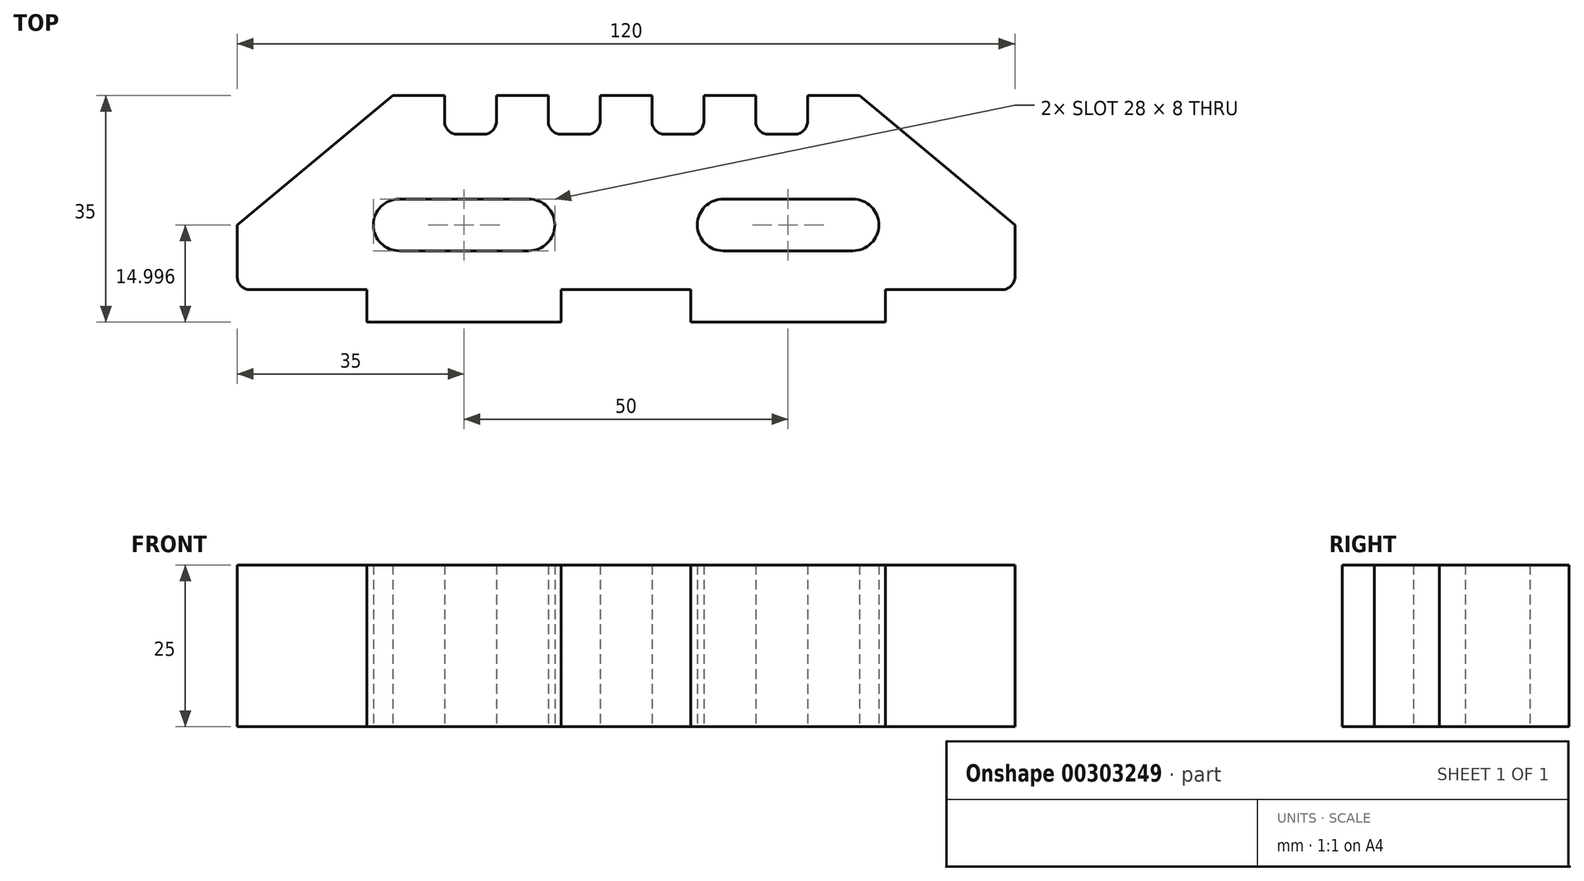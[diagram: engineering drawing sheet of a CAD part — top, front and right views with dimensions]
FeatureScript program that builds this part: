
annotation { "Feature Type Name" : "Feature", "Feature Type Description" : "" }
export const myFeature = defineFeature(function(context is Context, id is Id, definition is map)
    precondition{}
    {
        {
            var Q0;
            Q0=qCreatedBy(makeId("Top.planeOp"),FACE);
            var sketch = newSketch(context, id + "F0", { "sketchPlane" : qUnion([Q0])});
            skLineSegment(sketch, "E0", {"start": v(-58, -43.37) * mm, "end": v(-40, -43.37) * mm});
            skLineSegment(sketch, "E1", {"start": v(-40, -43.37) * mm, "end": v(-40, -48.37) * mm});
            skLineSegment(sketch, "E2", {"start": v(-40, -48.37) * mm, "end": v(-10, -48.37) * mm});
            skLineSegment(sketch, "E3", {"start": v(-10, -48.37) * mm, "end": v(-10, -43.37) * mm});
            skLineSegment(sketch, "E4", {"start": v(-10, -43.37) * mm, "end": v(10, -43.37) * mm});
            skLineSegment(sketch, "E5", {"start": v(10, -43.37) * mm, "end": v(10, -48.37) * mm});
            skLineSegment(sketch, "E6", {"start": v(10, -48.37) * mm, "end": v(40, -48.37) * mm});
            skLineSegment(sketch, "E7", {"start": v(40, -48.37) * mm, "end": v(40, -43.37) * mm});
            skLineSegment(sketch, "E8", {"start": v(40, -43.37) * mm, "end": v(58, -43.37) * mm});
            skLineSegment(sketch, "E9", {"start": v(60, -41.37) * mm, "end": v(60, -33.37) * mm});
            skLineSegment(sketch, "E10", {"start": v(36, -13.37) * mm, "end": v(60, -33.37) * mm});
            skLineSegment(sketch, "E11", {"start": v(36, -13.37) * mm, "end": v(28, -13.37) * mm});
            skLineSegment(sketch, "E12", {"start": v(28, -13.37) * mm, "end": v(28, -17.37) * mm});
            skLineSegment(sketch, "E13", {"start": v(26, -19.37) * mm, "end": v(22, -19.37) * mm});
            skLineSegment(sketch, "E14", {"start": v(20, -17.37) * mm, "end": v(20, -13.37) * mm});
            skLineSegment(sketch, "E15", {"start": v(20, -13.37) * mm, "end": v(12, -13.37) * mm});
            skLineSegment(sketch, "E16", {"start": v(12, -13.37) * mm, "end": v(12, -17.37) * mm});
            skLineSegment(sketch, "E17", {"start": v(10, -19.37) * mm, "end": v(6, -19.37) * mm});
            skLineSegment(sketch, "E18", {"start": v(4, -17.37) * mm, "end": v(4, -13.37) * mm});
            skLineSegment(sketch, "E19", {"start": v(4, -13.37) * mm, "end": v(-4, -13.37) * mm});
            skLineSegment(sketch, "E20", {"start": v(-4, -13.37) * mm, "end": v(-4, -17.37) * mm});
            skLineSegment(sketch, "E21", {"start": v(-6, -19.37) * mm, "end": v(-10, -19.37) * mm});
            skLineSegment(sketch, "E22", {"start": v(-12, -17.37) * mm, "end": v(-12, -13.37) * mm});
            skLineSegment(sketch, "E23", {"start": v(-12, -13.37) * mm, "end": v(-20, -13.37) * mm});
            skLineSegment(sketch, "E24", {"start": v(-20, -13.37) * mm, "end": v(-20, -17.37) * mm});
            skLineSegment(sketch, "E25", {"start": v(-22, -19.37) * mm, "end": v(-26, -19.37) * mm});
            skLineSegment(sketch, "E26", {"start": v(-28, -17.37) * mm, "end": v(-28, -13.37) * mm});
            skLineSegment(sketch, "E27", {"start": v(-28, -13.37) * mm, "end": v(-36, -13.37) * mm});
            skLineSegment(sketch, "E28", {"start": v(-60, -41.37) * mm, "end": v(-60, -33.37) * mm});
            skLineSegment(sketch, "E29", {"start": v(-60, -33.37) * mm, "end": v(-36, -13.37) * mm});
            skPoint(sketch, "E30.visualSharp", {"position": v(-28, -19.37) * mm});
            skArc(sketch, "E30.filletArc", {"start": v(-28, -17.37) * mm, "mid": v(-27.41, -18.79) * mm, "end": v(-26, -19.37) * mm});
            skPoint(sketch, "E31.visualSharp", {"position": v(-20, -19.37) * mm});
            skArc(sketch, "E31.filletArc", {"start": v(-22, -19.37) * mm, "mid": v(-20.59, -18.79) * mm, "end": v(-20, -17.37) * mm});
            skPoint(sketch, "E32.visualSharp", {"position": v(-12, -19.37) * mm});
            skArc(sketch, "E32.filletArc", {"start": v(-12, -17.37) * mm, "mid": v(-11.41, -18.79) * mm, "end": v(-10, -19.37) * mm});
            skPoint(sketch, "E33.visualSharp", {"position": v(-4, -19.37) * mm});
            skArc(sketch, "E33.filletArc", {"start": v(-6, -19.37) * mm, "mid": v(-4.59, -18.79) * mm, "end": v(-4, -17.37) * mm});
            skPoint(sketch, "E34.visualSharp", {"position": v(4, -19.37) * mm});
            skArc(sketch, "E34.filletArc", {"start": v(4, -17.37) * mm, "mid": v(4.59, -18.79) * mm, "end": v(6, -19.37) * mm});
            skPoint(sketch, "E35.visualSharp", {"position": v(12, -19.37) * mm});
            skArc(sketch, "E35.filletArc", {"start": v(10, -19.37) * mm, "mid": v(11.41, -18.79) * mm, "end": v(12, -17.37) * mm});
            skPoint(sketch, "E36.visualSharp", {"position": v(20, -19.37) * mm});
            skArc(sketch, "E36.filletArc", {"start": v(20, -17.37) * mm, "mid": v(20.59, -18.79) * mm, "end": v(22, -19.37) * mm});
            skPoint(sketch, "E37.visualSharp", {"position": v(28, -19.37) * mm});
            skArc(sketch, "E37.filletArc", {"start": v(26, -19.37) * mm, "mid": v(27.41, -18.79) * mm, "end": v(28, -17.37) * mm});
            skPoint(sketch, "E38.visualSharp", {"position": v(60, -43.37) * mm});
            skArc(sketch, "E38.filletArc", {"start": v(58, -43.37) * mm, "mid": v(59.41, -42.79) * mm, "end": v(60, -41.37) * mm});
            skPoint(sketch, "E39.visualSharp", {"position": v(-60, -43.37) * mm});
            skArc(sketch, "E39.filletArc", {"start": v(-60, -41.37) * mm, "mid": v(-59.41, -42.79) * mm, "end": v(-58, -43.37) * mm});
            skLineSegment(sketch, "E40", {"start": v(11, -29.37) * mm, "end": v(39, -29.37) * mm});
            skLineSegment(sketch, "E41", {"start": v(35, -29.37) * mm, "end": v(15, -29.37) * mm});
            skLineSegment(sketch, "E42", {"start": v(11, -33.37) * mm, "end": v(11, -33.37) * mm});
            skLineSegment(sketch, "E43", {"start": v(15, -37.37) * mm, "end": v(35, -37.37) * mm});
            skLineSegment(sketch, "E44", {"start": v(39, -33.37) * mm, "end": v(39, -33.37) * mm});
            skPoint(sketch, "E45.orphan", {"position": v(25, -29.37) * mm});
            skPoint(sketch, "E46.start.orphan", {"position": v(25, -48.37) * mm});
            skPoint(sketch, "E47.orphan", {"position": v(0, -29.37) * mm});
            skPoint(sketch, "E48.orphan", {"position": v(0, -43.37) * mm});
            skPoint(sketch, "E49.end.orphan", {"position": v(0, -13.37) * mm});
            skLineSegment(sketch, "E50", {"start": v(-11, -29.37) * mm, "end": v(-39, -29.37) * mm});
            skLineSegment(sketch, "E51", {"start": v(-39, -33.37) * mm, "end": v(-39, -33.37) * mm});
            skLineSegment(sketch, "E52", {"start": v(-35, -29.37) * mm, "end": v(-15, -29.37) * mm});
            skLineSegment(sketch, "E53", {"start": v(-11, -33.37) * mm, "end": v(-11, -33.37) * mm});
            skPoint(sketch, "E54.end.orphan", {"position": v(0, -37.37) * mm});
            skPoint(sketch, "E55.orphan", {"position": v(-25, -48.37) * mm});
            skPoint(sketch, "E56.orphan", {"position": v(-45.9, -29.37) * mm});
            skPoint(sketch, "E57.trimOffspring.end.orphan", {"position": v(-45.9, -37.37) * mm});
            skLineSegment(sketch, "E58", {"start": v(-35, -37.37) * mm, "end": v(-15, -37.37) * mm});
            skPoint(sketch, "E59.visualSharp", {"position": v(-11, -29.37) * mm});
            skArc(sketch, "E59.filletArc", {"start": v(-11, -33.37) * mm, "mid": v(-12.17, -30.55) * mm, "end": v(-15, -29.37) * mm});
            skPoint(sketch, "E60.visualSharp", {"position": v(-11, -37.37) * mm});
            skArc(sketch, "E60.filletArc", {"start": v(-15, -37.37) * mm, "mid": v(-12.17, -36.2) * mm, "end": v(-11, -33.37) * mm});
            skPoint(sketch, "E61.visualSharp", {"position": v(-39, -37.37) * mm});
            skArc(sketch, "E61.filletArc", {"start": v(-39, -33.37) * mm, "mid": v(-37.83, -36.2) * mm, "end": v(-35, -37.37) * mm});
            skPoint(sketch, "E62.visualSharp", {"position": v(-39, -29.37) * mm});
            skArc(sketch, "E62.filletArc", {"start": v(-35, -29.37) * mm, "mid": v(-37.83, -30.55) * mm, "end": v(-39, -33.37) * mm});
            skPoint(sketch, "E63.visualSharp", {"position": v(11, -29.37) * mm});
            skArc(sketch, "E63.filletArc", {"start": v(15, -29.37) * mm, "mid": v(12.17, -30.55) * mm, "end": v(11, -33.37) * mm});
            skPoint(sketch, "E64.visualSharp", {"position": v(11, -37.37) * mm});
            skArc(sketch, "E64.filletArc", {"start": v(11, -33.37) * mm, "mid": v(12.17, -36.2) * mm, "end": v(15, -37.37) * mm});
            skPoint(sketch, "E65.visualSharp", {"position": v(39, -37.37) * mm});
            skArc(sketch, "E65.filletArc", {"start": v(35, -37.37) * mm, "mid": v(37.83, -36.2) * mm, "end": v(39, -33.37) * mm});
            skPoint(sketch, "E66.visualSharp", {"position": v(39, -29.37) * mm});
            skArc(sketch, "E66.filletArc", {"start": v(39, -33.37) * mm, "mid": v(37.83, -30.55) * mm, "end": v(35, -29.37) * mm});
            skSolve(sketch);
        }
        {
            var Q0;
            Q0=makeQuery(id+"F0.imprint","IMPRINT",FACE,{"disambiguationData":[TD([[makeQuery(id+"F0.imprint","IMPRINT",EDGE,{"derivedFrom":sQuery(id+"F0.wireOp",EDGE,"E0")}),1.0]])]});
            extrude(context, id + "F1", {"entities" : qUnion([Q0]), "depth" : 25 * mm});
        }
    });
